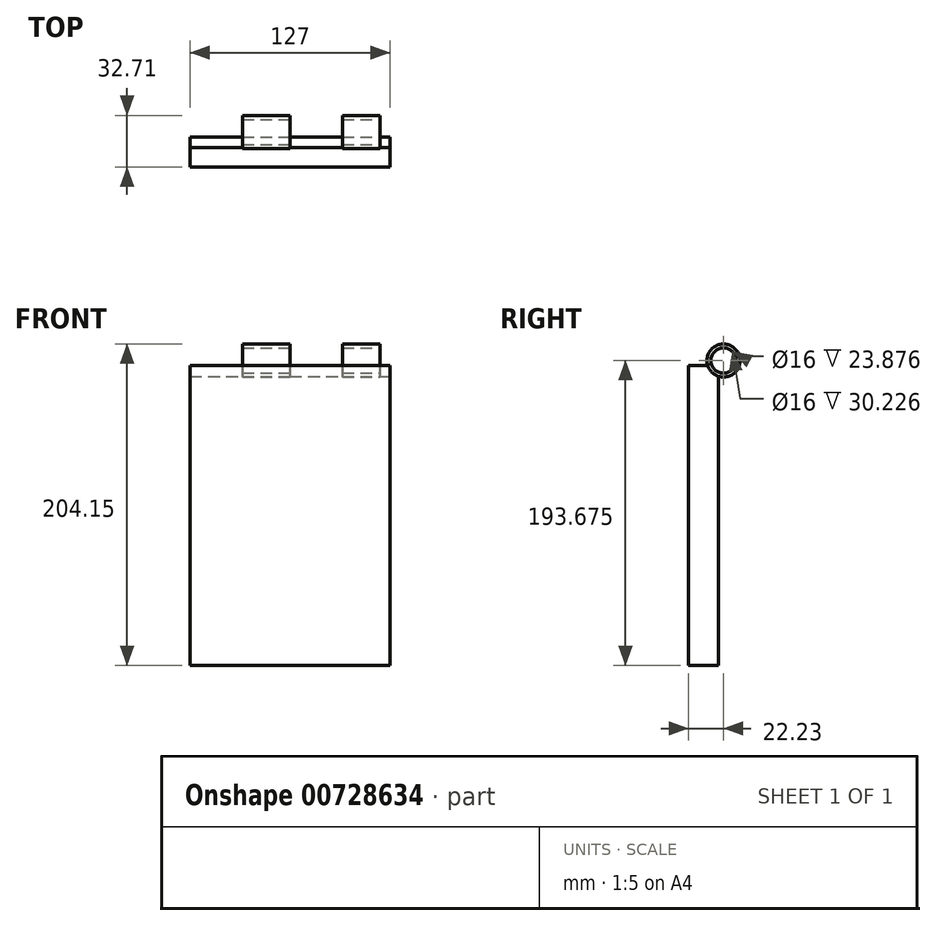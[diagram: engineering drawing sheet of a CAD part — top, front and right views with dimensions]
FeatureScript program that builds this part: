
annotation { "Feature Type Name" : "Feature", "Feature Type Description" : "" }
export const myFeature = defineFeature(function(context is Context, id is Id, definition is map)
    precondition{}
    {
        {
            var Q0;
            Q0=qCreatedBy(makeId("Front.planeOp"),FACE);
            var sketch = newSketch(context, id + "F0", { "sketchPlane" : qUnion([Q0])});
            skLineSegment(sketch, "E0.bottom", {"start": v(-63.5, 95.25) * mm, "end": v(63.5, 95.25) * mm});
            skLineSegment(sketch, "E0.top", {"start": v(-63.5, -95.25) * mm, "end": v(63.5, -95.25) * mm});
            skLineSegment(sketch, "E0.left", {"start": v(-63.5, 95.25) * mm, "end": v(-63.5, -95.25) * mm});
            skLineSegment(sketch, "E0.right", {"start": v(63.5, 95.25) * mm, "end": v(63.5, -95.25) * mm});
            skPoint(sketch, "E0.middle", {"position": v(0, 0) * mm});
            skSolve(sketch);
        }
        {
            var Q0;
            Q0=qSketchRegion(id+"F0",true);
            extrude(context, id + "F1", {"entities" : qUnion([Q0]), "endBound" : BoundingType.SYMMETRIC, "depth" : 19.05 * mm, "offsetDistance" : 25.4 * mm});
        }
        {
            var Q0;
            Q0=qCreatedBy(makeId("Right.planeOp"),FACE);
            var sketch = newSketch(context, id + "F2", { "sketchPlane" : qUnion([Q0])});
            skCircle(sketch, "E1", {"center": v(12.7, 98.43) * mm, "radius": 10.48 * mm});
            skCircle(sketch, "E2", {"center": v(12.7, 98.43) * mm, "radius": 8 * mm});
            skSolve(sketch);
        }
        {
            var Q0;
            Q0=qSketchRegion(id+"F2",true);
            var Q1;
            Q1=makeQuery(id+"F2.imprint","IMPRINT",FACE,{"disambiguationData":[TD([[makeQuery(id+"F2.imprint","IMPRINT",EDGE,{"derivedFrom":sQuery(id+"F2.wireOp",EDGE,"E2")}),1.0]])]});
            extrude(context, id + "F3", {"entities" : qUnion([Q0, Q1]), "operationType" : NewBodyOperationType.REMOVE, "endBound" : BoundingType.THROUGH_ALL, "oppositeDirection" : true, "depth" : 25.4 * mm, "offsetDistance" : 25.4 * mm, "hasSecondDirection" : true, "secondDirectionBound" : SecondDirectionBoundingType.THROUGH_ALL, "secondDirectionOppositeDirection" : false, "secondDirectionDepth" : 25.4 * mm});
        }
        {
            var Q0;
            Q0=qSketchRegion(id+"F2",true);
            var Q1;
            Q1=makeQuery(id+"F1.opExtrude","SWEPT_FACE",FACE,{"disambiguationData":[OSD([sQuery(id+"F0.wireOp",EDGE,"E0.right")])]});
            extrude(context, id + "F4", {"entities" : qUnion([Q0]), "operationType" : NewBodyOperationType.ADD, "oppositeDirection" : true, "depth" : 30.23 * mm, "offsetDistance" : 25.4 * mm});
        }
        {
            var Q0;
            {var subQ0=sQuery(id+"F0.wireOp",EDGE,"E0.right");Q0=makeQuery(id+"F4.boolean.opBoolean","MERGE",FACE,{"derivedFrom":[makeQuery(id+"F1.opExtrude","SWEPT_FACE",FACE,{"disambiguationData":[OSD([subQ0])]}),makeQuery(id+"F4.opExtrude","CAP_FACE",FACE,{"disambiguationData":[OSD([subQ0])],"isStart":true})]});}
            var sketch = newSketch(context, id + "F5", { "sketchPlane" : qUnion([Q0])});
            skCircle(sketch, "E3", {"center": v(12.7, 98.42) * mm, "radius": 10.48 * mm});
            skCircle(sketch, "E4", {"center": v(12.7, 98.42) * mm, "radius": 8 * mm});
            skSolve(sketch);
        }
        {
            var Q0;
            Q0=qSketchRegion(id+"F5",true);
            extrude(context, id + "F6", {"entities" : qUnion([Q0]), "operationType" : NewBodyOperationType.ADD, "oppositeDirection" : true, "depth" : 30.23 * mm, "offsetDistance" : 25.4 * mm});
        }
        {
            var Q0;
            Q0 = qSketchRegion(id + "F5", true);
            extrude(context, id + "F7", {"entities" : qUnion([Q0]), "operationType" : NewBodyOperationType.REMOVE, "oppositeDirection" : true, "depth" : 6.35 * mm, "offsetDistance" : 25.4 * mm});
        }
    });
